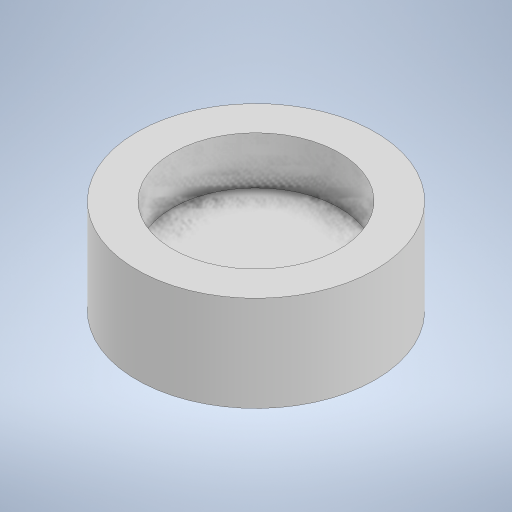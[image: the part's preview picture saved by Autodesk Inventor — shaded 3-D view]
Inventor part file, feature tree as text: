
AUTODESK INVENTOR PART (.ipt)
format: ipt  version: 2023 (Build 270158000, 158)  size: 226,816 bytes
history: native  units: mm
features: extrude x2, other x1, sketch x1
ambient origin geometry x8: Origin, YZ Plane, XZ Plane, XY Plane, X Axis, Y Axis, Z Axis, Center Point
bodies: Body1 (feature_tree)
feature tree (4):
  other  "솔리드1"
  sketch  "스케치1"
  extrude  "돌출1"  Depth=15.0mm
  extrude  "돌출2"  Depth=10.5mm
